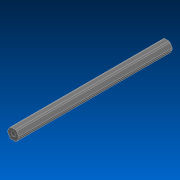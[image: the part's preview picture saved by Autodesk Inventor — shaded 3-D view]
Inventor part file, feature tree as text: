
AUTODESK INVENTOR PART (.ipt)
format: ipt  version: 2022.2 (Build 262287000, 287)  size: 121,856 bytes
history: native  units: in
note: dims shown in document units (in); Inventor stores cm internally (conversion verified against a paired STEP export)
features: extrude x1, sketch x1, other x1
ambient origin geometry x8: Origin, YZ Plane, XZ Plane, XY Plane, X Axis, Y Axis, Z Axis, Center Point
bodies: Solid1 (feature_tree)
feature tree (3):
  extrude  "Extrusion1"  TaperAngle=0.0deg  [1 undecoded]
  sketch  "Sketch1"  dims[d0=28.5in d1=0.0in]
  other  "Cut-Extrude2"
note: 1 required parameter value undecoded (feature->parameter linkage not recoverable at this tier; creation-order binding heuristic only, values carry confidence <= 0.55)
